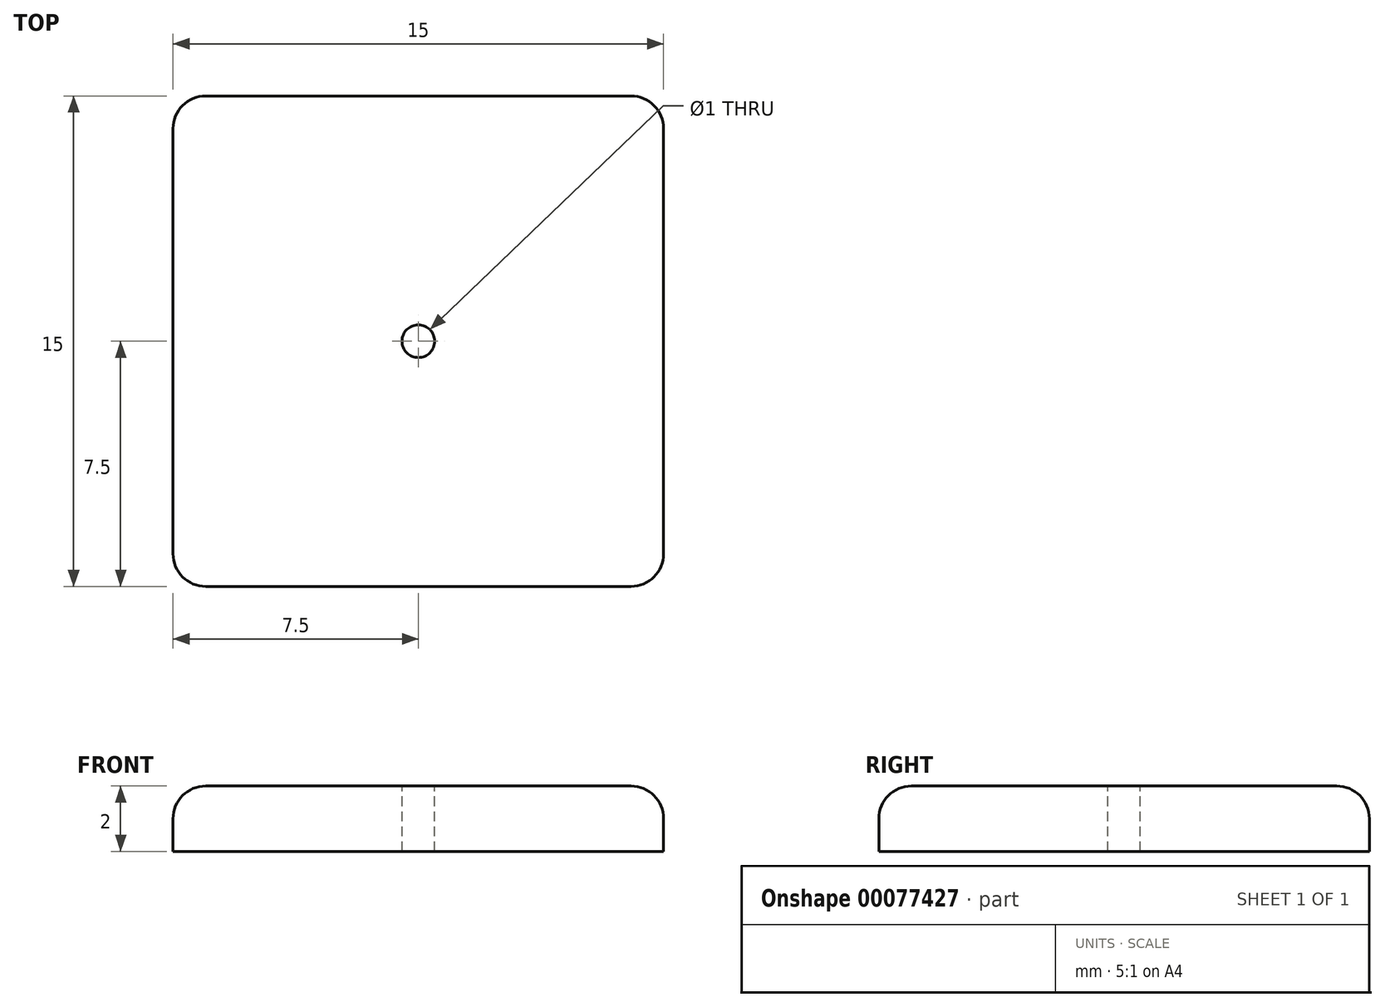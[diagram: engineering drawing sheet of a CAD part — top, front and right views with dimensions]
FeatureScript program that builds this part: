
annotation { "Feature Type Name" : "Feature", "Feature Type Description" : "" }
export const myFeature = defineFeature(function(context is Context, id is Id, definition is map)
    precondition{}
    {
        {
            var Q0;
            Q0=qCreatedBy(makeId("Top.planeOp"),FACE);
            var sketch = newSketch(context, id + "F0", { "sketchPlane" : qUnion([Q0])});
            skLineSegment(sketch, "E0.bottom", {"start": v(0, 0) * mm, "end": v(-15, 0) * mm});
            skLineSegment(sketch, "E0.top", {"start": v(0, 15) * mm, "end": v(-15, 15) * mm});
            skLineSegment(sketch, "E0.left", {"start": v(0, 0) * mm, "end": v(0, 15) * mm});
            skLineSegment(sketch, "E0.right", {"start": v(-15, 0) * mm, "end": v(-15, 15) * mm});
            skPoint(sketch, "E1", {"position": v(-7.5, 7.5) * mm});
            skSolve(sketch);
        }
        {
            var Q0;
            Q0=qSketchRegion(id+"F0",true);
            extrude(context, id + "F1", {"entities" : qUnion([Q0]), "depth" : 2 * mm});
        }
        {
            var Q0;
            Q0=makeQuery(id+"F1.opExtrude","CAP_FACE",FACE,{"disambiguationData":[OSD([sQuery(id+"F0.wireOp",EDGE,"E0.bottom"),sQuery(id+"F0.wireOp",EDGE,"E0.top"),sQuery(id+"F0.wireOp",EDGE,"E0.left"),sQuery(id+"F0.wireOp",EDGE,"E0.right")])],"isStart":false});
            var sketch = newSketch(context, id + "F2", { "sketchPlane" : qUnion([Q0])});
            skPoint(sketch, "E2", {"position": v(-7.5, 7.5) * mm});
            skPoint(sketch, "E2.positionSnap0", {"position": v(0, 7.5) * mm});
            skPoint(sketch, "E2.positionSnap1", {"position": v(-7.5, 0) * mm});
            skSolve(sketch);
        }
        {
            var Q0;
            Q0=sQuery(id+"F2.wireOp",VERTEX,"E2");
            var Q1;
            Q1=makeQuery(id+"F1.opExtrude","SWEPT_BODY",BODY,{"disambiguationData":[OSD([sQuery(id+"F0.wireOp",EDGE,"E0.bottom"),sQuery(id+"F0.wireOp",EDGE,"E0.top"),sQuery(id+"F0.wireOp",EDGE,"E0.left"),sQuery(id+"F0.wireOp",EDGE,"E0.right")])]});
            hole(context, id + "F3", {"style" : HoleStyle.SIMPLE, "endStyle" : HoleEndStyle.THROUGH, "holeDiameter" : 1 * mm, "locations" : qUnion([Q0]), "scope" : qUnion([Q1]), "isTappedThrough" : true});
        }
        {
            var Q0;
            Q0=makeQuery(id+"F1.opExtrude","CAP_EDGE",EDGE,{"disambiguationData":[OSD([sQuery(id+"F0.wireOp",EDGE,"E0.bottom")])],"isStart":false});
            var Q1;
            Q1=makeQuery(id+"F1.opExtrude","CAP_EDGE",EDGE,{"disambiguationData":[OSD([sQuery(id+"F0.wireOp",EDGE,"E0.right")])],"isStart":false});
            var Q2;
            Q2=makeQuery(id+"F1.opExtrude","CAP_EDGE",EDGE,{"disambiguationData":[OSD([sQuery(id+"F0.wireOp",EDGE,"E0.top")])],"isStart":false});
            var Q3;
            Q3=makeQuery(id+"F1.opExtrude","CAP_EDGE",EDGE,{"disambiguationData":[OSD([sQuery(id+"F0.wireOp",EDGE,"E0.left")])],"isStart":false});
            var Q4;
            Q4=makeQuery(id+"F1.opExtrude","SWEPT_EDGE",EDGE,{"disambiguationData":[OSD([sQuery(id+"F0.wireOp",EDGE,"E0.bottom"),sQuery(id+"F0.wireOp",EDGE,"E0.left")])]});
            var Q5;
            Q5=makeQuery(id+"F1.opExtrude","SWEPT_EDGE",EDGE,{"disambiguationData":[OSD([sQuery(id+"F0.wireOp",EDGE,"E0.bottom"),sQuery(id+"F0.wireOp",EDGE,"E0.right")])]});
            var Q6;
            Q6=makeQuery(id+"F1.opExtrude","SWEPT_EDGE",EDGE,{"disambiguationData":[OSD([sQuery(id+"F0.wireOp",EDGE,"E0.top"),sQuery(id+"F0.wireOp",EDGE,"E0.left")])]});
            var Q7;
            Q7=makeQuery(id+"F1.opExtrude","SWEPT_EDGE",EDGE,{"disambiguationData":[OSD([sQuery(id+"F0.wireOp",EDGE,"E0.top"),sQuery(id+"F0.wireOp",EDGE,"E0.right")])]});
            fillet(context, id + "F4", {"entities" : qUnion([Q0, Q1, Q2, Q3, Q4, Q5, Q6, Q7]), "radius" : 1 * mm, "tangentPropagation" : true, "allowEdgeOverflow" : false});
        }
    });
